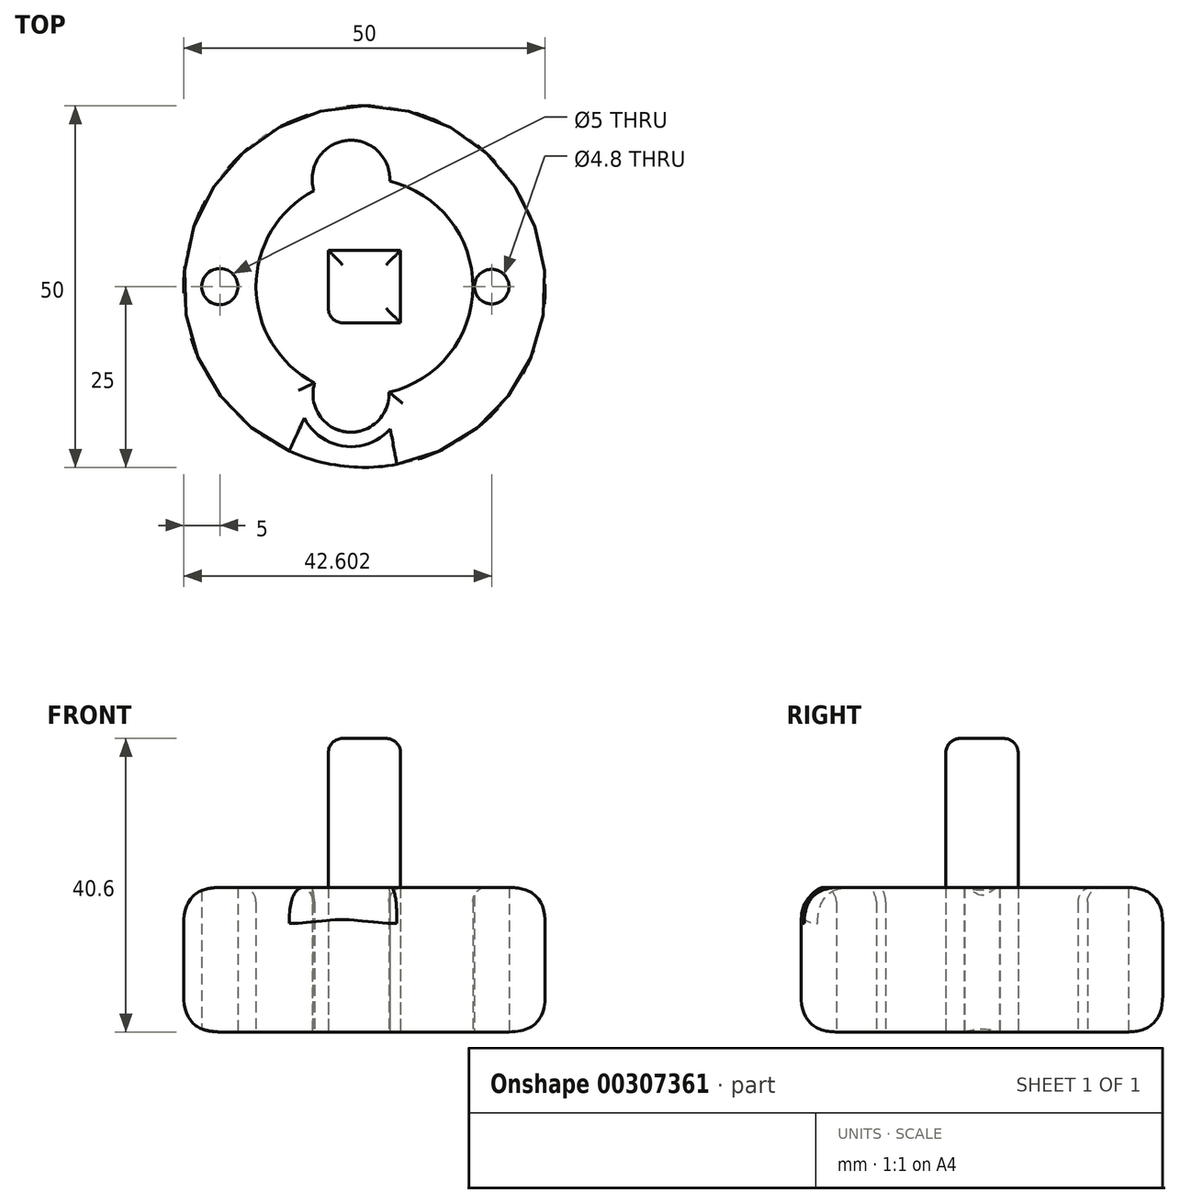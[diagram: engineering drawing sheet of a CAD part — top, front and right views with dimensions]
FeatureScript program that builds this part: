
annotation { "Feature Type Name" : "Feature", "Feature Type Description" : "" }
export const myFeature = defineFeature(function(context is Context, id is Id, definition is map)
    precondition{}
    {
        {
            var Q0;
            Q0=qCreatedBy(makeId("Top.planeOp"),FACE);
            var sketch = newSketch(context, id + "F0", { "sketchPlane" : qUnion([Q0])});
            skCircle(sketch, "E0", {"center": v(0, 0) * mm, "radius": 25 * mm});
            skCircle(sketch, "E1", {"center": v(0, 0) * mm, "radius": 20 * mm, "construction": true});
            skArc(sketch, "E2", {"start": v(3.38, -14.61) * mm, "mid": v(14.98, 0.77) * mm, "end": v(1.87, 14.88) * mm});
            skCircle(sketch, "E3", {"center": v(-17.6, 45.87) * mm, "radius": 10 * mm});
            skCircle(sketch, "E4", {"center": v(-20, 0) * mm, "radius": 2.5 * mm});
            skCircle(sketch, "E5", {"center": v(17.6, 0) * mm, "radius": 2.4 * mm});
            skArc(sketch, "E6", {"start": v(-6.89, -13.33) * mm, "mid": v(-2.52, -20.1) * mm, "end": v(3.38, -14.61) * mm});
            skArc(sketch, "E7", {"start": v(3.5, 14.59) * mm, "mid": v(-2.53, 20.21) * mm, "end": v(-6.99, 13.27) * mm});
            skPoint(sketch, "E7.centerSnap0", {"position": v(1.87, 14.88) * mm});
            skArc(sketch, "E8.trimOffspring", {"start": v(-6.99, 13.27) * mm, "mid": v(-15, -0.06) * mm, "end": v(-6.89, -13.33) * mm});
            skLineSegment(sketch, "E9", {"start": v(-17.3, 55.87) * mm, "end": v(-17.6, 45.87) * mm, "construction": true});
            skLineSegment(sketch, "E10", {"start": v(-17.6, 45.87) * mm, "end": v(-17.45, 50.87) * mm, "construction": true});
            skLineSegment(sketch, "E11.bottom", {"start": v(-17.45, 50.87) * mm, "end": v(0, 50.87) * mm});
            skLineSegment(sketch, "E11.top", {"start": v(-17.45, 45.87) * mm, "end": v(0, 45.87) * mm});
            skLineSegment(sketch, "E11.left", {"start": v(-17.45, 50.87) * mm, "end": v(-17.45, 45.87) * mm});
            skLineSegment(sketch, "E11.right", {"start": v(0, 50.87) * mm, "end": v(0, 45.87) * mm});
            skCircle(sketch, "E12", {"center": v(0, 0) * mm, "radius": 8.7 * mm});
            skLineSegment(sketch, "E13.bottom", {"start": v(5, -5) * mm, "end": v(-5, -5) * mm});
            skLineSegment(sketch, "E13.top", {"start": v(5, 5) * mm, "end": v(-5, 5) * mm});
            skLineSegment(sketch, "E13.left", {"start": v(5, -5) * mm, "end": v(5, 5) * mm});
            skLineSegment(sketch, "E13.right", {"start": v(-5, -5) * mm, "end": v(-5, 5) * mm});
            skSolve(sketch);
        }
        {
            var Q0;
            Q0=makeQuery(id+"F0.imprint","IMPRINT",FACE,{"disambiguationData":[TD([[makeQuery(id+"F0.imprint","IMPRINT",EDGE,{"derivedFrom":sQuery(id+"F0.wireOp",EDGE,"E0")}),1.0]])]});
            extrude(context, id + "F1", {"entities" : qUnion([Q0]), "depth" : 20 * mm});
        }
        {
            var Q0;
            Q0=makeQuery(id+"F0.imprint","IMPRINT",FACE,{"disambiguationData":[TD([[makeQuery(id+"F0.imprint","IMPRINT",EDGE,{"derivedFrom":sQuery(id+"F0.wireOp",EDGE,"E13.bottom")}),-1.0]])]});
            extrude(context, id + "F2", {"entities" : qUnion([Q0]), "depth" : 40.6 * mm});
        }
        {
            var Q0;
            Q0=makeQuery(id+"F2.opExtrude","CAP_EDGE",EDGE,{"disambiguationData":[OSD([sQuery(id+"F0.wireOp",EDGE,"E13.bottom")])],"isStart":false});
            var Q1;
            Q1=makeQuery(id+"F2.opExtrude","CAP_EDGE",EDGE,{"disambiguationData":[OSD([sQuery(id+"F0.wireOp",EDGE,"E13.top")])],"isStart":false});
            var Q2;
            Q2=makeQuery(id+"F2.opExtrude","CAP_EDGE",EDGE,{"disambiguationData":[OSD([sQuery(id+"F0.wireOp",EDGE,"E13.left")])],"isStart":false});
            var Q3;
            Q3=makeQuery(id+"F2.opExtrude","CAP_EDGE",EDGE,{"disambiguationData":[OSD([sQuery(id+"F0.wireOp",EDGE,"E13.right")])],"isStart":false});
            var Q4;
            Q4=makeQuery(id+"F2.opExtrude","SWEPT_EDGE",EDGE,{"disambiguationData":[OSD([sQuery(id+"F0.wireOp",EDGE,"E13.bottom"),sQuery(id+"F0.wireOp",EDGE,"E13.right")])]});
            var Q5;
            Q5=makeQuery(id+"F1.opExtrude","CAP_EDGE",EDGE,{"disambiguationData":[OSD([sQuery(id+"F0.wireOp",EDGE,"E2")])],"isStart":false});
            var Q6;
            Q6=makeQuery(id+"F1.opExtrude","CAP_EDGE",EDGE,{"disambiguationData":[OSD([sQuery(id+"F0.wireOp",EDGE,"E8.trimOffspring")])],"isStart":false});
            var Q7;
            Q7=makeQuery(id+"F1.opExtrude","CAP_EDGE",EDGE,{"disambiguationData":[OSD([sQuery(id+"F0.wireOp",EDGE,"E6")])],"isStart":false});
            fillet(context, id + "F3", {"entities" : qUnion([Q0, Q1, Q2, Q3, Q4, Q5, Q6, Q7]), "radius" : 2 * mm, "tangentPropagation" : true, "allowEdgeOverflow" : false});
        }
        {
            var Q0;
            Q0=makeQuery(id+"F1.opExtrude","CAP_EDGE",EDGE,{"disambiguationData":[OSD([sQuery(id+"F0.wireOp",EDGE,"E0")])],"isStart":false});
            var Q1;
            Q1=makeQuery(id+"F1.opExtrude","CAP_EDGE",EDGE,{"disambiguationData":[OSD([sQuery(id+"F0.wireOp",EDGE,"E0")])],"isStart":true});
            fillet(context, id + "F4", {"entities" : qUnion([Q0, Q1]), "radius" : 5 * mm, "tangentPropagation" : true, "rho" : 0.5, "crossSection" : FilletCrossSection.CONIC, "allowEdgeOverflow" : false});
        }
    });
